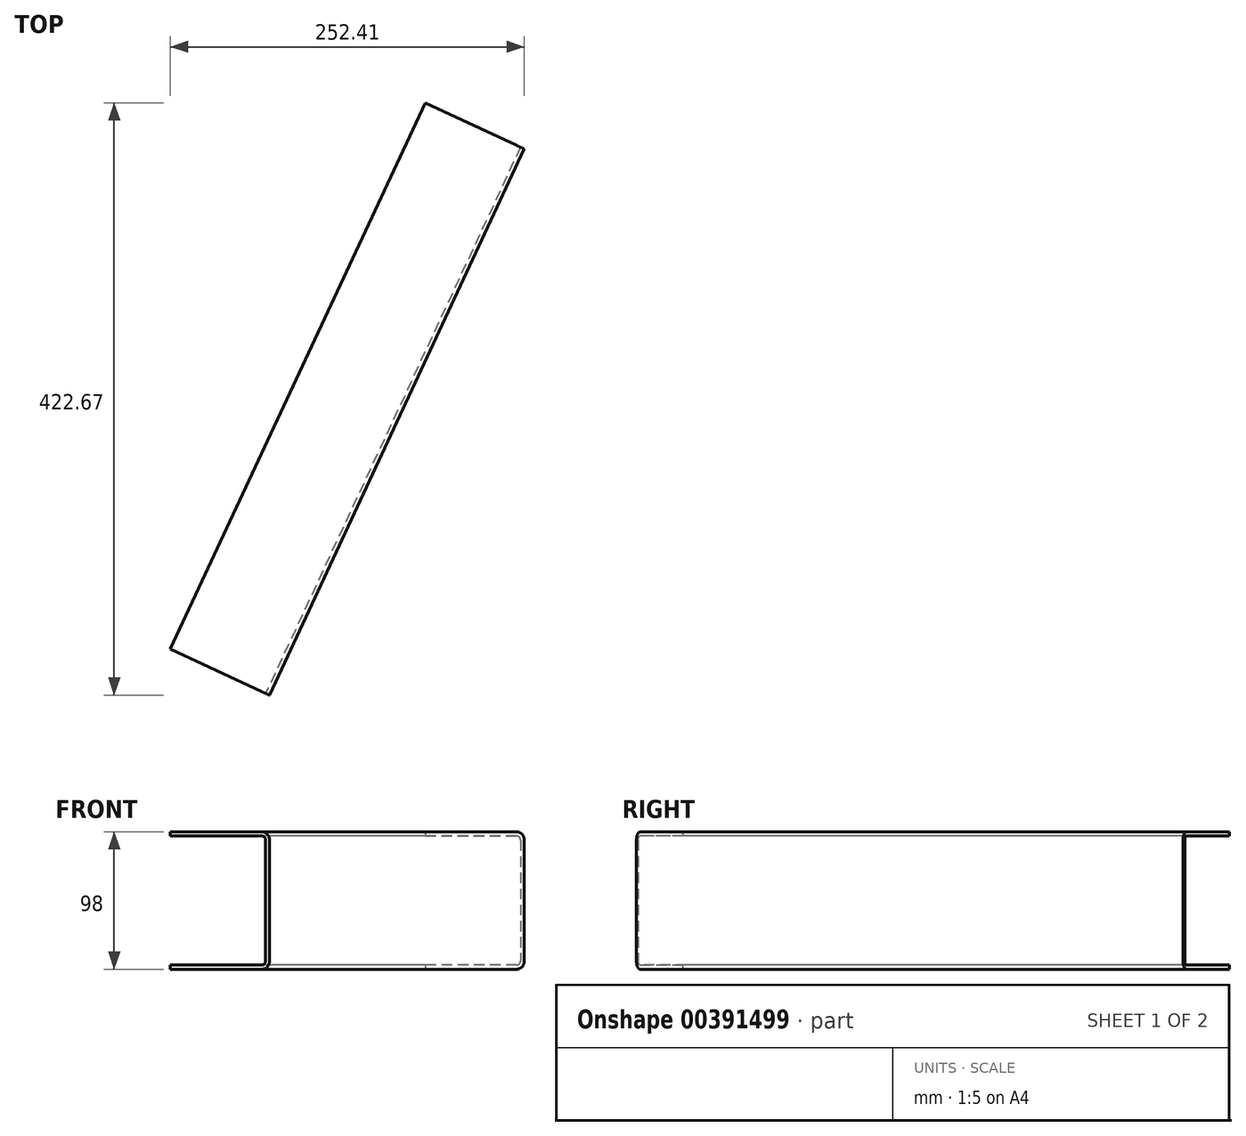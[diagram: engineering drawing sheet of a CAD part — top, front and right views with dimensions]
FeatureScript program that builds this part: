
annotation { "Feature Type Name" : "Feature", "Feature Type Description" : "" }
export const myFeature = defineFeature(function(context is Context, id is Id, definition is map)
    precondition{}
    {
        {
            var Q0;
            Q0=qCreatedBy(makeId("Front.planeOp"),FACE);
            var sketch = newSketch(context, id + "F0", { "sketchPlane" : qUnion([Q0])});
            skLineSegment(sketch, "E0", {"start": v(-43.73, 38.55) * mm, "end": v(28.27, 38.55) * mm});
            skLineSegment(sketch, "E1", {"start": v(31.27, 35.55) * mm, "end": v(31.27, -50.45) * mm});
            skLineSegment(sketch, "E2", {"start": v(28.27, -53.45) * mm, "end": v(-43.73, -53.45) * mm});
            skPoint(sketch, "E3.visualSharp", {"position": v(31.27, 38.55) * mm});
            skArc(sketch, "E3.filletArc", {"start": v(31.27, 35.55) * mm, "mid": v(30.39, 37.67) * mm, "end": v(28.27, 38.55) * mm});
            skPoint(sketch, "E4.visualSharp", {"position": v(31.27, -53.45) * mm});
            skArc(sketch, "E4.filletArc", {"start": v(28.27, -53.45) * mm, "mid": v(30.39, -52.57) * mm, "end": v(31.27, -50.45) * mm});
            skLineSegment(sketch, "E5.0", {"start": v(-43.73, 41.55) * mm, "end": v(28.27, 41.55) * mm});
            skLineSegment(sketch, "E6.0", {"start": v(34.27, 35.55) * mm, "end": v(34.27, -50.45) * mm});
            skLineSegment(sketch, "E7.0", {"start": v(28.27, -56.45) * mm, "end": v(-43.73, -56.45) * mm});
            skArc(sketch, "E8.0", {"start": v(34.27, 35.55) * mm, "mid": v(32.5, 39.8) * mm, "end": v(28.27, 41.55) * mm});
            skArc(sketch, "E9.0", {"start": v(28.27, -56.45) * mm, "mid": v(32.5, -54.7) * mm, "end": v(34.27, -50.45) * mm});
            skLineSegment(sketch, "E10", {"start": v(-43.73, -53.45) * mm, "end": v(-43.73, -56.45) * mm});
            skLineSegment(sketch, "E11", {"start": v(-43.73, 41.55) * mm, "end": v(-43.73, 38.55) * mm});
            skSolve(sketch);
        }
        {
            var Q0;
            Q0=makeQuery(id+"F0.imprint","IMPRINT",FACE,{"disambiguationData":[TD([[makeQuery(id+"F0.imprint","IMPRINT",EDGE,{"derivedFrom":sQuery(id+"F0.wireOp",EDGE,"E0")}),1.0]])]});
            extrude(context, id + "F1", {"entities" : qUnion([Q0]), "oppositeDirection" : true, "depth" : 430 * mm});
        }
        {
            var Q0;
            Q0=makeQuery(id+"F1.opExtrude","SWEPT_BODY",BODY,{"disambiguationData":[OSD([sQuery(id+"F0.wireOp",EDGE,"E0"),sQuery(id+"F0.wireOp",EDGE,"E1"),sQuery(id+"F0.wireOp",EDGE,"E2"),sQuery(id+"F0.wireOp",EDGE,"E3.filletArc"),sQuery(id+"F0.wireOp",EDGE,"E4.filletArc"),sQuery(id+"F0.wireOp",EDGE,"E5.0"),sQuery(id+"F0.wireOp",EDGE,"E6.0"),sQuery(id+"F0.wireOp",EDGE,"E7.0"),sQuery(id+"F0.wireOp",EDGE,"E8.0"),sQuery(id+"F0.wireOp",EDGE,"E9.0"),sQuery(id+"F0.wireOp",EDGE,"E10"),sQuery(id+"F0.wireOp",EDGE,"E11")])]});
            var Q1;
            Q1=sQuery(id+"F0.wireOp",EDGE,"E11");
            transform(context, id + "F2", {"entities" : qUnion([Q0]), "transformType" : TransformType.ROTATION, "transformAxis" : qUnion([Q1]), "angle" : 25 * degree, "makeCopy" : false});
        }
    });
